# Revit family: Rahmenkassette Schwerlast, blind, RKSL, Nenngröße 250-3, Belastungsklasse 1
name_source: partatom
category: Generic Models
revit_build: Autodesk Revit 2015 (Build: 20140606_1530(x64)
units: mm (PartAtom-declared; Revit-internal decimal feet)

## types (4) — shared parameters
Manufacturer = OBO Bettermann
Material = Stainless Steel
URL = http://www.obo-bettermann.com
Width = 324 mm  [stored 1.06299 ft]
Width 1 = 288 mm  [stored 0.944882 ft]

## per-type parameters (varying)
| type | Cut depth | GTIN | Height | Height 1 | Manufacturer Art.No. |
| RK SL1 V2 20 | 5 mm  [stored 0.0164042 ft] | 4012195105824 | 20 mm  [stored 0.0656168 ft] | 18 mm  [stored 0.0590551 ft] | 7405892 |
| RK SL1 V2 25 | 5 mm  [stored 0.0164042 ft] | 4012195105831 | 25 mm  [stored 0.082021 ft] | 23 mm  [stored 0.0754593 ft] | 7405896 |
| RK SL1 V2 30 | 0 mm  [stored 0 ft] | 4012195105848 | 30 mm  [stored 0.0984252 ft] | 28 mm  [stored 0.0918635 ft] | 7405900 |
| RK SL1 V2 40 | 5 mm  [stored 0.0164042 ft] | 4012195105886 | 40 mm  [stored 0.131234 ft] | 38 mm  [stored 0.124672 ft] | 7405908 |

note: column(s) folded — value = type name in every type: Article Type

note: [stored X ft] marks values corroborated as IEEE doubles in the binary element streams (Revit-internal decimal feet)

## geometry (parser evidence)
native form markers: Sweep x2
no freeform markers — native parametric forms only
